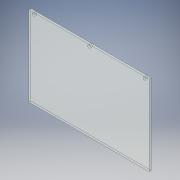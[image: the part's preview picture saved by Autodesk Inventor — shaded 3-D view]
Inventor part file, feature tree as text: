
AUTODESK INVENTOR PART (.ipt)
format: ipt  version: 2019 (Build 230136000, 136)  size: 111,104 bytes
history: native  units: mm
features: extrude x2, sketch x2
ambient origin geometry x8: Origin, YZ Plane, XZ Plane, XY Plane, X Axis, Y Axis, Z Axis, Center Point
bodies: Solid1 (feature_tree)
feature tree (4):
  extrude  "Extrusion1"  Depth=300.0mm
  extrude  "Extrusion2"  Depth=200.0mm
  sketch  "Sketch1"  dims[d0=200.0mm d1=300.0mm]
  sketch  "Sketch3"  dims[d2=142.857143mm d3=200.0mm d4=5.0mm d5=0.0mm d6=7.0mm d7=7.0mm d8=7.0mm d9=12.0mm d10=12.0mm d11=150.0mm d12=5.0mm d13=5.0mm d14=5.0mm d15=10.0mm d16=0.0mm]
